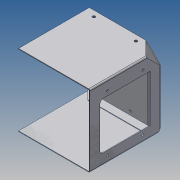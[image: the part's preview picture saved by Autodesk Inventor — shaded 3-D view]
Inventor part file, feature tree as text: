
AUTODESK INVENTOR PART (.ipt)
format: ipt  version: 2017 (Build 210142000, 142)  size: 427,008 bytes
history: native  units: mm
features: other x11, sketch x6, extrude x4, sheet_metal_op x4, hole x2, plane x1
ambient origin geometry x8: Origin, YZ Plane, XZ Plane, XY Plane, X Axis, Y Axis, Z Axis, Center Point
bodies: Solid1 (feature_tree)
feature tree (28):
  plane  "Work Plane1"
  extrude  "Extrusion1"  Depth=1.0mm TaperAngle=0.0deg
  sketch  "Sketch2"  dims[d4=100.0mm d5=1.0mm]
  sheet_metal_op  "Face1"
  other  "Pliegue1"
  sheet_metal_op  "Face2"
  other  "Pestaña1"
  sketch  "Boceto5"  dims[d10=19.9mm d12=99.8mm]
  other  "Cara3"
  extrude  "Extrusion2"  Depth=1.0mm
  extrude  "Extrusion3"  Depth=1.0mm
  extrude  "Extrusion4"  Depth=1.0mm
  hole  "Hole2"  [1 undecoded]
  sketch  "Sketch1"  dims[d0=50.0mm d2=1.0mm d3=0.0mm]
  other  "Plate1"
  sheet_metal_op  "Bend1"
  sketch  "Sketch3"  dims[d6=1.0mm d7=0.5mm]
  other  "Plate2"
  sheet_metal_op  "Bend2"
  sketch  "Boceto4"  dims[d8=2.0mm d9=1.0mm]
  other  "Placa3"
  other  "Doblez3"
  other  "Esquina1"
  other  "Placa4"
  other  "Doblez4"
  sketch  "Sketch6"  dims[d13=20.0mm d14=20.0mm d15=20.0mm d16=20.0mm d17=1.0mm d18=1.0mm d19=0.5mm d20=2.0mm d21=1.0mm d22=100.0mm d23=49.9mm d24=1.0mm d25=0.5mm d26=2.0mm d27=1.0mm d28=15.0mm d29=90.0deg d30=1.0mm d31=4.0mm d32=1.0mm d33=1.0mm d34=1.0mm d35=70.0mm d36=4.0mm d37=65.0mm d38=35.0mm d39=1.0mm d40=0.5mm d41=2.0mm d42=1.0mm d43=90.0deg d44=1.0mm d45=100.0mm d46=50.0mm d47=100.0mm d48=3.5mm d49=3.5mm d50=1.0mm d51=1.0mm d52=0.5mm d53=2.0mm d54=1.0mm d55=3.5mm d56=3.5mm d57=50.0mm d58=100.0mm d59=3.5mm d60=3.5mm d61=50.0mm d62=14.0mm d63=14.0mm d64=3.0mm d65=12.0mm d66=50.0mm d67=4.0mm d68=6.0mm d69=76.014719mm d70=6.0mm d71=6.0mm d72=10.0mm d73=0.0mm d74=10.0mm d75=0.0mm d76=10.0mm d77=0.0mm d78=12.0mm d79=45.0deg d80=12.0mm d81=3.4544mm d82=6.0mm d83=4.0mm d84=2.0mm d85=90.0deg d86=8.0mm d87=0.0mm]
  hole  "Hole1"  [1 undecoded]
  other  "Definición1"
note: 2 required parameter values undecoded (feature->parameter linkage not recoverable at this tier; creation-order binding heuristic only, values carry confidence <= 0.55)
